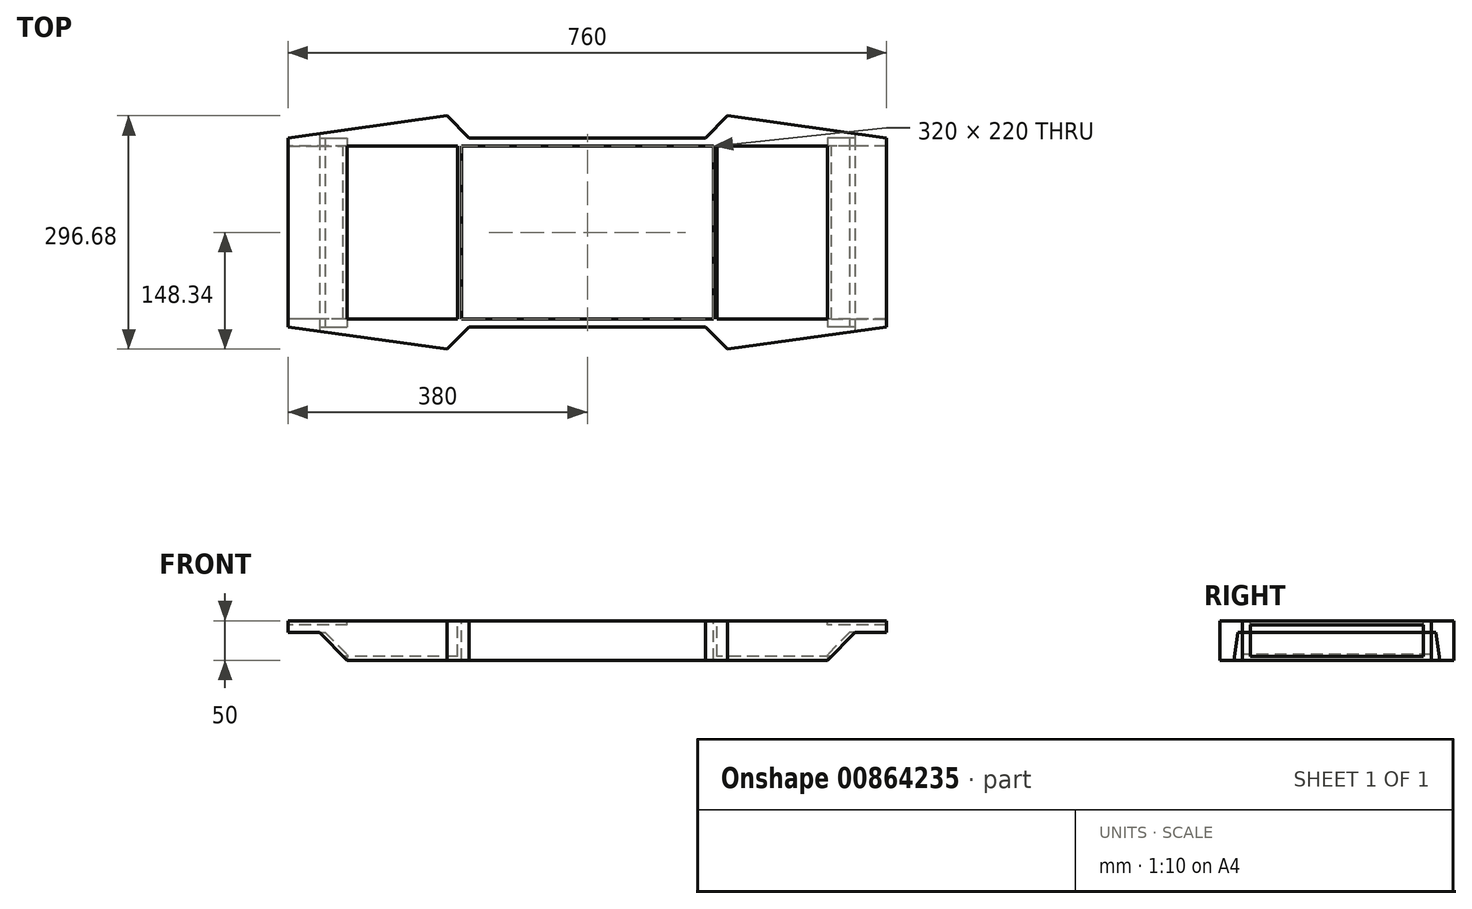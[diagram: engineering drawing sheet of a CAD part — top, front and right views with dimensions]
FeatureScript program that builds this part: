
annotation { "Feature Type Name" : "Feature", "Feature Type Description" : "" }
export const myFeature = defineFeature(function(context is Context, id is Id, definition is map)
    precondition{}
    {
        {
            var Q0;
            Q0=qCreatedBy(makeId("Top.planeOp"),FACE);
            var sketch = newSketch(context, id + "F0", { "sketchPlane" : qUnion([Q0])});
            skLineSegment(sketch, "E0", {"start": v(-380, 120) * mm, "end": v(-380, -120) * mm});
            skLineSegment(sketch, "E1", {"start": v(380, 120) * mm, "end": v(380, -120) * mm});
            skLineSegment(sketch, "E2", {"start": v(150, -120) * mm, "end": v(-150, -120) * mm});
            skLineSegment(sketch, "E3", {"start": v(-150, 120) * mm, "end": v(150, 120) * mm});
            skLineSegment(sketch, "E4", {"start": v(-160, 110) * mm, "end": v(160, 110) * mm, "construction": true});
            skLineSegment(sketch, "E5", {"start": v(160, 110) * mm, "end": v(160, -110) * mm, "construction": true});
            skLineSegment(sketch, "E6", {"start": v(160, -110) * mm, "end": v(-160, -110) * mm, "construction": true});
            skLineSegment(sketch, "E7", {"start": v(-160, -110) * mm, "end": v(-160, 110) * mm, "construction": true});
            skLineSegment(sketch, "E8.0", {"start": v(-150, -110) * mm, "end": v(-150, 110) * mm, "construction": true});
            skLineSegment(sketch, "E9.0", {"start": v(150, 110) * mm, "end": v(150, -110) * mm, "construction": true});
            skLineSegment(sketch, "E10", {"start": v(-150, -110) * mm, "end": v(-150, -120) * mm, "construction": true});
            skLineSegment(sketch, "E11", {"start": v(-150, 110) * mm, "end": v(-150, 120) * mm, "construction": true});
            skLineSegment(sketch, "E12", {"start": v(-150, 120) * mm, "end": v(-178.34, 148.34) * mm});
            skLineSegment(sketch, "E13", {"start": v(-380, 120) * mm, "end": v(-178.34, 148.34) * mm});
            skPoint(sketch, "E14.endSnap0", {"position": v(0, 110) * mm});
            skLineSegment(sketch, "E15.MirrorCS", {"start": v(150, 120) * mm, "end": v(178.34, 148.34) * mm});
            skLineSegment(sketch, "E16.MirrorCS", {"start": v(380, 120) * mm, "end": v(178.34, 148.34) * mm});
            skLineSegment(sketch, "E17.MirrorCS", {"start": v(-150, -120) * mm, "end": v(-178.34, -148.34) * mm, "construction": true});
            skLineSegment(sketch, "E18.MirrorCS", {"start": v(-380, -120) * mm, "end": v(-178.34, -148.34) * mm});
            skLineSegment(sketch, "E19.MirrorCS", {"start": v(150, -120) * mm, "end": v(178.34, -148.34) * mm});
            skLineSegment(sketch, "E20.MirrorCS", {"start": v(-150, -120) * mm, "end": v(-178.34, -148.34) * mm});
            skLineSegment(sketch, "E21.MirrorCS", {"start": v(380, -120) * mm, "end": v(178.34, -148.34) * mm});
            skSolve(sketch);
        }
        {
            var Q0;
            Q0=makeQuery(id+"F0.imprint","IMPRINT",FACE,{"disambiguationData":[TD([[makeQuery(id+"F0.imprint","IMPRINT",EDGE,{"derivedFrom":sQuery(id+"F0.wireOp",EDGE,"E0")}),1.0]])]});
            extrude(context, id + "F1", {"entities" : qUnion([Q0]), "depth" : 50 * mm, "offsetDistance" : 25 * mm});
        }
        {
            var Q0;
            Q0=makeQuery(id+"F1.opExtrude","SWEPT_FACE",FACE,{"disambiguationData":[OSD([sQuery(id+"F0.wireOp",EDGE,"E2")])]});
            var sketch = newSketch(context, id + "F2", { "sketchPlane" : qUnion([Q0])});
            skLineSegment(sketch, "E22", {"start": v(-380, 35) * mm, "end": v(-340, 35) * mm});
            skLineSegment(sketch, "E23", {"start": v(-340, 35) * mm, "end": v(-305, 0) * mm});
            skLineSegment(sketch, "E24", {"start": v(-380, 35) * mm, "end": v(-380, 0) * mm});
            skLineSegment(sketch, "E25", {"start": v(-380, 0) * mm, "end": v(-305, 0) * mm});
            skLineSegment(sketch, "E26.MirrorCS", {"start": v(380, 0) * mm, "end": v(305, 0) * mm});
            skLineSegment(sketch, "E27.MirrorCS", {"start": v(380, 35) * mm, "end": v(380, 0) * mm});
            skLineSegment(sketch, "E28.MirrorCS", {"start": v(380, 35) * mm, "end": v(340, 35) * mm});
            skLineSegment(sketch, "E29.MirrorCS", {"start": v(340, 35) * mm, "end": v(305, 0) * mm});
            skSolve(sketch);
        }
        {
            var Q0;
            Q0=makeQuery(id+"F1.opExtrude","SWEPT_FACE",FACE,{"disambiguationData":[OSD([sQuery(id+"F0.wireOp",EDGE,"E0")])]});
            var sketch = newSketch(context, id + "F3", { "sketchPlane" : qUnion([Q0])});
            skLineSegment(sketch, "E30.0", {"start": v(-110, 45) * mm, "end": v(110, 45) * mm});
            skLineSegment(sketch, "E31.0", {"start": v(-110, 5) * mm, "end": v(110, 5) * mm});
            skLineSegment(sketch, "E32.0", {"start": v(-110, 5) * mm, "end": v(-110, 45) * mm});
            skLineSegment(sketch, "E33.0", {"start": v(110, 45) * mm, "end": v(110, 5) * mm});
            skSolve(sketch);
        }
        {
            var Q0;
            Q0=makeQuery(id+"F3.imprint","IMPRINT",FACE,{"disambiguationData":[TD([[makeQuery(id+"F3.imprint","IMPRINT",EDGE,{"derivedFrom":sQuery(id+"F3.wireOp",EDGE,"E30.0")}),-1.0]])]});
            extrude(context, id + "F4", {"entities" : qUnion([Q0]), "operationType" : NewBodyOperationType.REMOVE, "oppositeDirection" : true, "depth" : 760 * mm, "offsetDistance" : 25 * mm});
        }
        {
            var Q0;
            Q0=makeQuery(id+"F2.imprint","IMPRINT",FACE,{"disambiguationData":[TD([[makeQuery(id+"F2.imprint","IMPRINT",EDGE,{"derivedFrom":sQuery(id+"F2.wireOp",EDGE,"E26.MirrorCS")}),-1.0]])]});
            var Q1;
            Q1=makeQuery(id+"F2.imprint","IMPRINT",FACE,{"disambiguationData":[TD([[makeQuery(id+"F2.imprint","IMPRINT",EDGE,{"derivedFrom":sQuery(id+"F2.wireOp",EDGE,"E22")}),-1.0]])]});
            extrude(context, id + "F5", {"entities" : qUnion([Q0, Q1]), "operationType" : NewBodyOperationType.REMOVE, "oppositeDirection" : true, "depth" : 240 * mm, "offsetDistance" : 25 * mm});
        }
        {
            var Q0;
            Q0=makeQuery(id+"F1.opExtrude","CAP_FACE",FACE,{"disambiguationData":[OSD([sQuery(id+"F0.wireOp",EDGE,"E0"),sQuery(id+"F0.wireOp",EDGE,"E1"),sQuery(id+"F0.wireOp",EDGE,"E2"),sQuery(id+"F0.wireOp",EDGE,"E3")])],"isStart":false});
            var sketch = newSketch(context, id + "F6", { "sketchPlane" : qUnion([Q0])});
            skLineSegment(sketch, "E34", {"start": v(-140, 90) * mm, "end": v(140, 90) * mm});
            skLineSegment(sketch, "E35", {"start": v(140, 90) * mm, "end": v(140, -90) * mm});
            skLineSegment(sketch, "E36", {"start": v(140, -90) * mm, "end": v(-140, -90) * mm});
            skLineSegment(sketch, "E37", {"start": v(-140, -90) * mm, "end": v(-140, 90) * mm});
            skLineSegment(sketch, "E38", {"start": v(160, 110) * mm, "end": v(160, -110) * mm});
            skLineSegment(sketch, "E39", {"start": v(-160, 110) * mm, "end": v(-160, -110) * mm});
            skLineSegment(sketch, "E40", {"start": v(-160, 110) * mm, "end": v(160, 110) * mm});
            skLineSegment(sketch, "E41", {"start": v(160, -110) * mm, "end": v(-160, -110) * mm});
            skSolve(sketch);
        }
        {
            var Q0;
            Q0=qSketchRegion(id+"F6",true);
            extrude(context, id + "F7", {"entities" : qUnion([Q0]), "operationType" : NewBodyOperationType.REMOVE, "oppositeDirection" : true, "depth" : 50 * mm, "offsetDistance" : 25 * mm});
        }
        {
            var Q0;
            Q0=qSketchRegion(id+"F2",true);
            extrude(context, id + "F8", {"entities" : qUnion([Q0]), "operationType" : NewBodyOperationType.REMOVE, "endBound" : BoundingType.SYMMETRIC, "oppositeDirection" : true, "depth" : 871.86 * mm, "offsetDistance" : 25 * mm});
        }
        {
            var Q0;
            {var subQ0=sQuery(id+"F0.wireOp",EDGE,"E18.MirrorCS");var subQ1=sQuery(id+"F0.wireOp",EDGE,"E16.MirrorCS");var subQ2=sQuery(id+"F0.wireOp",EDGE,"E15.MirrorCS");var subQ3=sQuery(id+"F0.wireOp",EDGE,"E13");var subQ4=sQuery(id+"F0.wireOp",EDGE,"E12");var subQ5=sQuery(id+"F0.wireOp",EDGE,"E19.MirrorCS");var subQ6=sQuery(id+"F0.wireOp",EDGE,"E0");var subQ7=sQuery(id+"F0.wireOp",EDGE,"E3");var subQ8=sQuery(id+"F0.wireOp",EDGE,"E1");var subQ9=sQuery(id+"F0.wireOp",EDGE,"E2");var subQ10=sQuery(id+"F0.wireOp",EDGE,"E20.MirrorCS");var subQ11=sQuery(id+"F0.wireOp",EDGE,"E21.MirrorCS");Q0=makeQuery(id+"F7.boolean.opBoolean","SPLIT",FACE,{"disambiguationData":[TD([makeQuery(id+"F1.opExtrude","SWEPT_FACE",FACE,{"disambiguationData":[OSD([subQ6])]})])],"derivedFrom":makeQuery(id+"F1.opExtrude","CAP_FACE",FACE,{"disambiguationData":[OSD([subQ6,subQ8,subQ9,subQ7,subQ4,subQ3,subQ2,subQ1,subQ0,subQ5,subQ10,subQ11])],"isStart":false})});}
            var sketch = newSketch(context, id + "F9", { "sketchPlane" : qUnion([Q0])});
            skLineSegment(sketch, "E42", {"start": v(-165, -110) * mm, "end": v(-305, -110) * mm});
            skLineSegment(sketch, "E43", {"start": v(-305, -110) * mm, "end": v(-305, 110) * mm});
            skLineSegment(sketch, "E44", {"start": v(-305, 110) * mm, "end": v(-165, 110) * mm});
            skLineSegment(sketch, "E45.0", {"start": v(-165, 110) * mm, "end": v(-165, -110) * mm});
            skLineSegment(sketch, "E46", {"start": v(0, 0) * mm, "end": v(0, 58.76) * mm});
            skLineSegment(sketch, "E47.MirrorCS", {"start": v(165, 110) * mm, "end": v(165, -110) * mm});
            skLineSegment(sketch, "E48.MirrorCS", {"start": v(165, -110) * mm, "end": v(305, -110) * mm});
            skLineSegment(sketch, "E49.MirrorCS", {"start": v(305, -110) * mm, "end": v(305, 110) * mm});
            skLineSegment(sketch, "E50.MirrorCS", {"start": v(305, 110) * mm, "end": v(165, 110) * mm});
            skSolve(sketch);
        }
        {
            var Q0;
            Q0=makeQuery(id+"F9.imprint","IMPRINT",FACE,{"disambiguationData":[TD([[makeQuery(id+"F9.imprint","IMPRINT",EDGE,{"derivedFrom":sQuery(id+"F9.wireOp",EDGE,"E42")}),-1.0]])]});
            var Q1;
            Q1=makeQuery(id+"F9.imprint","IMPRINT",FACE,{"disambiguationData":[TD([[makeQuery(id+"F9.imprint","IMPRINT",EDGE,{"derivedFrom":sQuery(id+"F9.wireOp",EDGE,"E47.MirrorCS")}),1.0]])]});
            extrude(context, id + "F10", {"entities" : qUnion([Q0, Q1]), "operationType" : NewBodyOperationType.REMOVE, "oppositeDirection" : true, "depth" : 10 * mm, "offsetDistance" : 25 * mm});
        }
        {
            var Q0;
            Q0=makeQuery(id+"F1.opExtrude","SWEPT_FACE",FACE,{"disambiguationData":[OSD([sQuery(id+"F0.wireOp",EDGE,"E2")])]});
            var sketch = newSketch(context, id + "F11", { "sketchPlane" : qUnion([Q0])});
            skLineSegment(sketch, "E51", {"start": v(-305, 50) * mm, "end": v(-305, 0) * mm});
            skLineSegment(sketch, "E52", {"start": v(-340, 50) * mm, "end": v(-340, 35) * mm});
            skLineSegment(sketch, "E53", {"start": v(-340, 35) * mm, "end": v(-305, 0) * mm});
            skLineSegment(sketch, "E54.0", {"start": v(-332.93, 35) * mm, "end": v(-305, 7.07) * mm});
            skLineSegment(sketch, "E55", {"start": v(-340, 35) * mm, "end": v(-332.93, 35) * mm});
            skLineSegment(sketch, "E56", {"start": v(0, 0) * mm, "end": v(0, 50) * mm});
            skLineSegment(sketch, "E57", {"start": v(-340, 35) * mm, "end": v(-346.55, 35) * mm});
            skLineSegment(sketch, "E58.MirrorCS", {"start": v(332.93, 35) * mm, "end": v(305, 7.07) * mm});
            skLineSegment(sketch, "E59.MirrorCS", {"start": v(340, 35) * mm, "end": v(305, 0) * mm});
            skLineSegment(sketch, "E60.MirrorCS", {"start": v(340, 35) * mm, "end": v(332.93, 35) * mm});
            skLineSegment(sketch, "E61", {"start": v(305, 7.07) * mm, "end": v(305, 0) * mm});
            skSolve(sketch);
        }
        {
            var Q0;
            {var subQ0=sQuery(id+"F11.wireOp",EDGE,"E53");Q0=makeQuery(id+"F11.imprint","IMPRINT",FACE,{"disambiguationData":[TD([[makeQuery(id+"F11.imprint","IMPRINT",EDGE,{"derivedFrom":subQ0}),1.0]])]});}
            var Q1;
            Q1=makeQuery(id+"F11.imprint","IMPRINT",FACE,{"disambiguationData":[TD([[makeQuery(id+"F11.imprint","IMPRINT",EDGE,{"derivedFrom":sQuery(id+"F11.wireOp",EDGE,"E58.MirrorCS")}),1.0]])]});
            extrude(context, id + "F12", {"entities" : qUnion([Q0, Q1]), "oppositeDirection" : true, "depth" : 240 * mm, "offsetDistance" : 25 * mm});
        }
        {
            var Q0;
            Q0=makeQuery(id+"F7.boolean.opBoolean","SPLIT",FACE,{"disambiguationData":[TD([makeQuery(id+"F7.opExtrude","SWEPT_FACE",FACE,{"disambiguationData":[OSD([sQuery(id+"F6.wireOp",EDGE,"E34")])]})])],"derivedFrom":makeQuery(id+"F1.opExtrude","CAP_FACE",FACE,{"disambiguationData":[OSD([sQuery(id+"F0.wireOp",EDGE,"E0"),sQuery(id+"F0.wireOp",EDGE,"E1"),sQuery(id+"F0.wireOp",EDGE,"E2"),sQuery(id+"F0.wireOp",EDGE,"E3"),sQuery(id+"F0.wireOp",EDGE,"E12"),sQuery(id+"F0.wireOp",EDGE,"E13"),sQuery(id+"F0.wireOp",EDGE,"E15.MirrorCS"),sQuery(id+"F0.wireOp",EDGE,"E16.MirrorCS"),sQuery(id+"F0.wireOp",EDGE,"E18.MirrorCS"),sQuery(id+"F0.wireOp",EDGE,"E19.MirrorCS"),sQuery(id+"F0.wireOp",EDGE,"E20.MirrorCS"),sQuery(id+"F0.wireOp",EDGE,"E21.MirrorCS")])],"isStart":false})});
            extrude(context, id + "F13", {"entities" : qUnion([Q0]), "operationType" : NewBodyOperationType.REMOVE, "oppositeDirection" : true, "depth" : 25 * mm, "offsetDistance" : 25 * mm});
        }
        {
            var Q0;
            Q0=makeQuery(id+"F7.boolean.opBoolean","SPLIT",FACE,{"disambiguationData":[TD([makeQuery(id+"F7.opExtrude","SWEPT_FACE",FACE,{"disambiguationData":[OSD([sQuery(id+"F6.wireOp",EDGE,"E34")])]})])],"derivedFrom":makeQuery(id+"F1.opExtrude","CAP_FACE",FACE,{"disambiguationData":[OSD([sQuery(id+"F0.wireOp",EDGE,"E0"),sQuery(id+"F0.wireOp",EDGE,"E1"),sQuery(id+"F0.wireOp",EDGE,"E2"),sQuery(id+"F0.wireOp",EDGE,"E3"),sQuery(id+"F0.wireOp",EDGE,"E12"),sQuery(id+"F0.wireOp",EDGE,"E13"),sQuery(id+"F0.wireOp",EDGE,"E15.MirrorCS"),sQuery(id+"F0.wireOp",EDGE,"E16.MirrorCS"),sQuery(id+"F0.wireOp",EDGE,"E18.MirrorCS"),sQuery(id+"F0.wireOp",EDGE,"E19.MirrorCS"),sQuery(id+"F0.wireOp",EDGE,"E20.MirrorCS"),sQuery(id+"F0.wireOp",EDGE,"E21.MirrorCS")])],"isStart":true})});
            extrude(context, id + "F14", {"entities" : qUnion([Q0]), "operationType" : NewBodyOperationType.REMOVE, "oppositeDirection" : true, "depth" : 25 * mm, "offsetDistance" : 25 * mm});
        }
        {
            var Q0;
            Q0=makeQuery(id+"F7.boolean.opBoolean","COPY",FACE,{"disambiguationData":[TD([makeQuery(id+"F4.boolean.opBoolean","COPY",FACE,{"derivedFrom":makeQuery(id+"F4.opExtrude","SWEPT_FACE",FACE,{"disambiguationData":[OSD([sQuery(id+"F3.wireOp",EDGE,"E30.0")])]})})])],"derivedFrom":makeQuery(id+"F7.opExtrude","SWEPT_FACE",FACE,{"disambiguationData":[OSD([sQuery(id+"F6.wireOp",EDGE,"E38")])]})});
            var sketch = newSketch(context, id + "F15", { "sketchPlane" : qUnion([Q0])});
            skLineSegment(sketch, "E62", {"start": v(-110, 45) * mm, "end": v(-110, 5) * mm});
            skLineSegment(sketch, "E63", {"start": v(-110, 45) * mm, "end": v(110, 45) * mm});
            skLineSegment(sketch, "E64", {"start": v(110, 45) * mm, "end": v(110, 5) * mm});
            skLineSegment(sketch, "E65", {"start": v(-110, 5) * mm, "end": v(110, 5) * mm});
            skSolve(sketch);
        }
        {
            var Q0;
            Q0=makeQuery(id+"F7.boolean.opBoolean","COPY",FACE,{"disambiguationData":[TD([makeQuery(id+"F4.boolean.opBoolean","COPY",FACE,{"derivedFrom":makeQuery(id+"F4.opExtrude","SWEPT_FACE",FACE,{"disambiguationData":[OSD([sQuery(id+"F3.wireOp",EDGE,"E31.0")])]})})])],"derivedFrom":makeQuery(id+"F7.opExtrude","SWEPT_FACE",FACE,{"disambiguationData":[OSD([sQuery(id+"F6.wireOp",EDGE,"E39")])]})});
            var sketch = newSketch(context, id + "F16", { "sketchPlane" : qUnion([Q0])});
            skLineSegment(sketch, "E66", {"start": v(-110, 5) * mm, "end": v(-110, 45) * mm});
            skLineSegment(sketch, "E67", {"start": v(-110, 5) * mm, "end": v(110, 5) * mm});
            skLineSegment(sketch, "E68", {"start": v(110, 5) * mm, "end": v(110, 45) * mm});
            skLineSegment(sketch, "E69", {"start": v(-110, 45) * mm, "end": v(110, 45) * mm});
            skSolve(sketch);
        }
        {
            var Q0;
            Q0 = qSketchRegion(id + "F16", true);
            extrude(context, id + "F17", {"entities" : qUnion([Q0]), "operationType" : NewBodyOperationType.ADD, "oppositeDirection" : true, "depth" : 5 * mm, "offsetDistance" : 25 * mm});
        }
        {
            var Q0;
            Q0=makeQuery(id+"F15.imprint","IMPRINT",FACE,{"disambiguationData":[TD([[makeQuery(id+"F15.imprint","IMPRINT",EDGE,{"derivedFrom":sQuery(id+"F15.wireOp",EDGE,"E62")}),1.0]])]});
            extrude(context, id + "F18", {"entities" : qUnion([Q0]), "operationType" : NewBodyOperationType.ADD, "oppositeDirection" : true, "depth" : 5 * mm, "offsetDistance" : 25 * mm});
        }
    });
